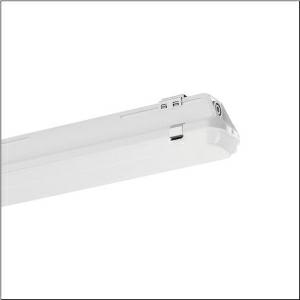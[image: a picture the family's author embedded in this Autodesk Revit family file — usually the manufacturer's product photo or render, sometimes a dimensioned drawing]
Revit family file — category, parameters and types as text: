
# Revit family: monsun_r__21_51fb10dp440c_e921
name_source: partatom
category: Lighting Fixtures
units: mm (PartAtom-declared; Revit-internal decimal feet)

## family parameters
Cut with Voids When Loaded = No
Host = Face
Light Source = No
Part Type = Normal
Room Calculation Point = No
Round Connector Dimension = Use Diameter
Shared = No

## types (1)
- --- (1 x LED, 4360 lm, 24.2 W, 4000K)
    Apparent Load = 24 VA
    CIE Flux Codes = 47 77 93 94 100
    Color Rendering = 80
    Color Temperature = 4000K
    Default Elevation = 1800 mm
    Description = Monsun® 21, damp-proof luminaire, chain hanger, primary optical cover: enclosure, of PMMA, light emission: direct distribution, primary light characteristic: symmetric, installation type: suspended mounting, surface-mounted, horizontal mounting, vertical mounting, LED, rated luminous flux: 4.360lm, luminous efficacy: 180lm/W, light colour: 840, colour temperature: 4000K, control gear: DALI 2, with terminal, 5-pole, max. 2.5mm², mains connection: 220..240V, AC, 50/60Hz, rated input power: 24W, housing, of glass-fibre reinforced polyester, uncoated, bright grey, incl. chain hanger, length: 1.590mm, width: 90mm, height: 88mm, clip for enclosure, of stainless steel (V2A), ceiling mounting element, of stainless steel (V2A), chain hanger, of stainless steel (V2A), protection rating (complete): IP66, insulation class (complete): insulation class I (protective earthing), certification: CE, ENEC, VDE, UKCA, protection symbol: D, impact resistance: IK04, permissible operating ambient temperature: -25..+35°C, standard: EN 50419, EN 60598-2-1, corresponds to IFS (International Featured Standards) requirements for safety and quality in the food industry, for indoor or canopied outdoor use, no direct snow, no direct sun, no direct rain, LABS conformity tested according to VDMA 24364:2018-05, contact your sales advisor before using the luminaires in applications with unclear chemical exposure, large temperature fluctuations or condensation-forming humidity, packaging unit: 1 piece
    Height = 89 mm
    Lamp = 1 x LED
    Lamp Light Flux = 4360 lm
    Lamp Power = 24.2 W
    Lamp count = 1
    Length = 1590 mm
    Luminous efficacy = 180 lm/W
    Manufacturer = Siteco
    ModVariant = No
    Model = 51FB10DP440C
    Mounting Place = Ceiling
    Mounting Type = Surface mounted
    Number of Poles = 1
    OnlyDefault = Yes
    Power Factor = 1
    Product Name = Monsun® 21
    Product group = damp-proof luminaire
    ProductGroupID = 301
    Protection Class = Protection class I
    Protection Degree = IP 66
    RLX_Detail_Level = 1
    RLX_Emergency_Light_Flux = 0 lm
    RLX_Emergency_Type = 0
    RLX_Emergency_Type_DB = No
    RlxData = <blob elided: 92221 chars, md5=8cbd1b0f>
    Socket = socket
    Standby Power = 0 W
    System Light Flux = 4360 lm
    System Power = 24 W
    Type Comments = factory setting: luminous flux: 100 % | dim-lin: 254 | 163 mA
    Type Image = l_1319656.jpg
    URL = http://relux.com
    VarID = @adj_052133
    Voltage = 0 V
    Weight = 0.00 kg
    Width = 90 mm

## geometry (parser evidence)
native form markers: Blend x4, Sweep x11
no freeform markers — native parametric forms only
